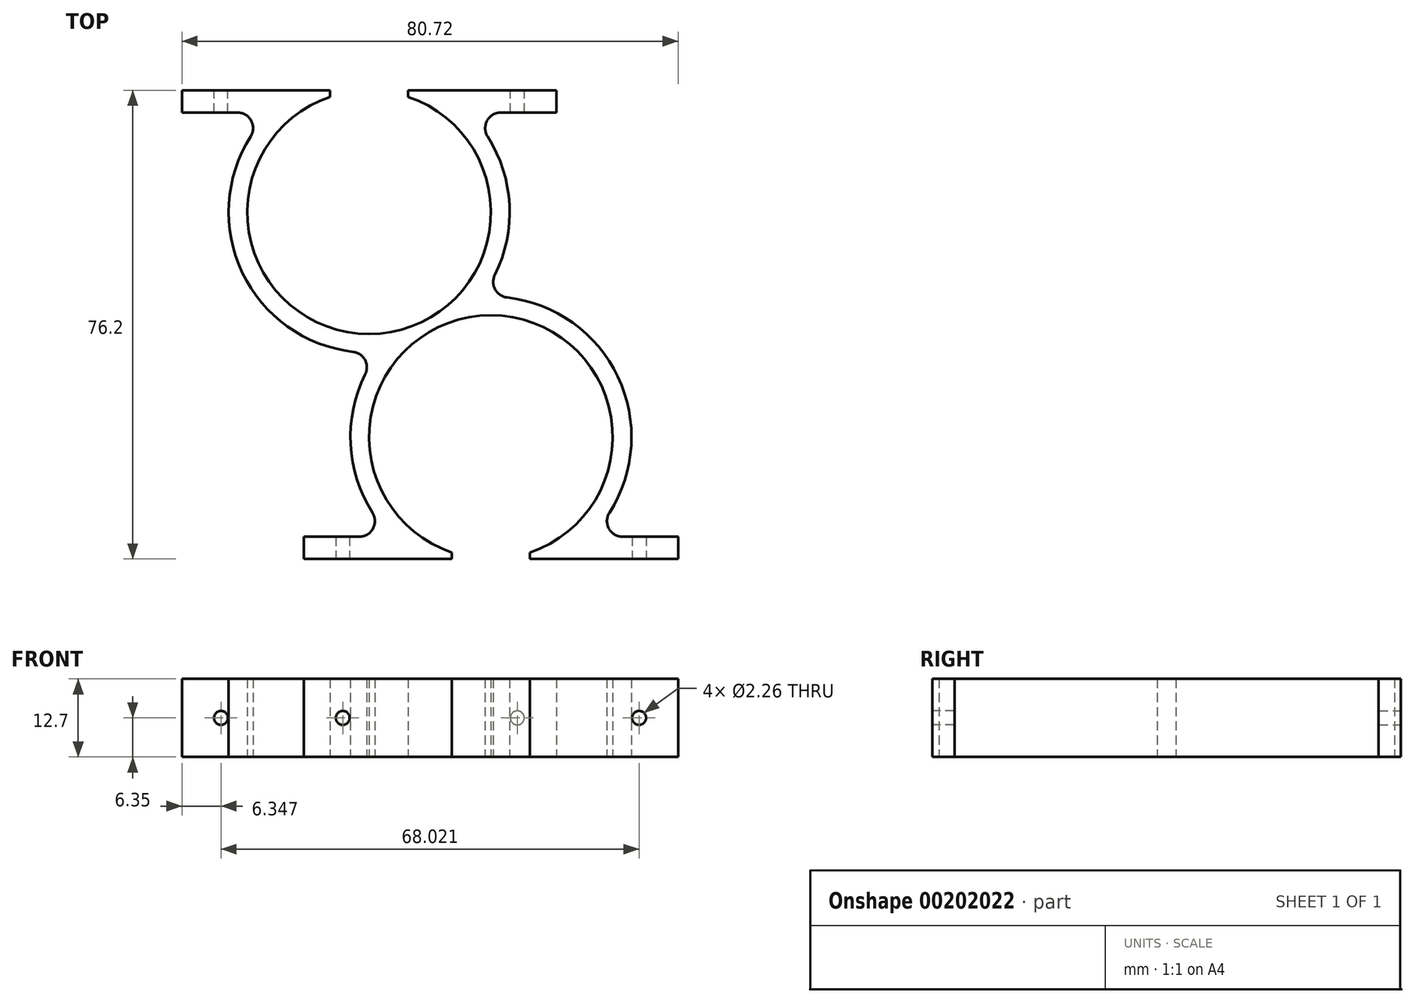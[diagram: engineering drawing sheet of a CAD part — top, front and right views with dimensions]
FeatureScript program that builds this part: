
annotation { "Feature Type Name" : "Feature", "Feature Type Description" : "" }
export const myFeature = defineFeature(function(context is Context, id is Id, definition is map)
    precondition{}
    {
        {
            var Q0;
            Q0=qCreatedBy(makeId("Top.planeOp"),FACE);
            var sketch = newSketch(context, id + "F0", { "sketchPlane" : qUnion([Q0])});
            skLineSegment(sketch, "E0.bottom", {"start": v(50.8, -38.1) * mm, "end": v(19.28, -38.1) * mm});
            skLineSegment(sketch, "E0.top", {"start": v(50.8, 38.1) * mm, "end": v(-0.53, 38.1) * mm});
            skLineSegment(sketch, "E0.left", {"start": v(50.8, -38.1) * mm, "end": v(50.8, 38.1) * mm});
            skLineSegment(sketch, "E0.right", {"start": v(-50.8, -38.1) * mm, "end": v(-50.8, 6.88) * mm});
            skPoint(sketch, "E0.middle", {"position": v(0, 0) * mm});
            skPoint(sketch, "E1.end.orphan", {"position": v(-30.99, 0) * mm});
            skLineSegment(sketch, "E2", {"start": v(-30.99, 38.1) * mm, "end": v(-30.99, 18.29) * mm});
            skArc(sketch, "E3", {"start": v(-37.34, 37.05) * mm, "mid": v(-30.99, -1.52) * mm, "end": v(-24.64, 37.05) * mm});
            skLineSegment(sketch, "E4", {"start": v(-50.8, -38.1) * mm, "end": v(-41.63, -38.1) * mm});
            skLineSegment(sketch, "E5", {"start": v(-11.18, -38.1) * mm, "end": v(-11.18, -18.29) * mm});
            skArc(sketch, "E6", {"start": v(-4.83, -37.05) * mm, "mid": v(-11.18, 1.52) * mm, "end": v(-17.53, -37.05) * mm});
            skArc(sketch, "E7.0", {"start": v(-10.53, 8.08) * mm, "mid": v(-8.16, 19.49) * mm, "end": v(-11.72, 30.58) * mm});
            skArc(sketch, "E8.0", {"start": v(-31.63, -8.08) * mm, "mid": v(-34, -19.49) * mm, "end": v(-30.45, -30.58) * mm});
            skArc(sketch, "E9.trimOffspring", {"start": v(8.1, -30.58) * mm, "mid": v(9.47, -8.47) * mm, "end": v(-8.55, 4.42) * mm});
            skArc(sketch, "E10.trimOffspring", {"start": v(-50.26, 30.58) * mm, "mid": v(-51.63, 8.47) * mm, "end": v(-33.61, -4.42) * mm});
            skPoint(sketch, "E11.visualSharp", {"position": v(-12.74, 4.52) * mm});
            skArc(sketch, "E11.filletArc", {"start": v(-10.53, 8.08) * mm, "mid": v(-10.5, 5.73) * mm, "end": v(-8.55, 4.42) * mm});
            skPoint(sketch, "E12.visualSharp", {"position": v(-29.42, -4.52) * mm});
            skArc(sketch, "E12.filletArc", {"start": v(-31.63, -8.08) * mm, "mid": v(-31.67, -5.73) * mm, "end": v(-33.61, -4.42) * mm});
            skLineSegment(sketch, "E13", {"start": v(-22.58, -38.1) * mm, "end": v(-22.58, -40.64) * mm});
            skLineSegment(sketch, "E14", {"start": v(-22.58, -40.64) * mm, "end": v(-40.26, -40.64) * mm});
            skLineSegment(sketch, "E15", {"start": v(-32.59, -34.49) * mm, "end": v(-41.63, -34.49) * mm});
            skLineSegment(sketch, "E16", {"start": v(-41.63, -34.49) * mm, "end": v(-41.63, -38.1) * mm});
            skLineSegment(sketch, "E17.MirrorCS", {"start": v(4.95, -34.49) * mm, "end": v(19.28, -34.49) * mm});
            skLineSegment(sketch, "E18.MirrorCS", {"start": v(10.24, -34.49) * mm, "end": v(19.28, -34.49) * mm});
            skLineSegment(sketch, "E19.MirrorCS", {"start": v(19.28, -34.49) * mm, "end": v(19.28, -38.1) * mm});
            skLineSegment(sketch, "E20.MirrorCS", {"start": v(28.45, -38.1) * mm, "end": v(19.28, -38.1) * mm});
            skPoint(sketch, "E21.orphan", {"position": v(-22.58, -34.49) * mm});
            skPoint(sketch, "E22.orphan", {"position": v(0.23, -34.49) * mm});
            skPoint(sketch, "E23.MirrorCS.start.orphan", {"position": v(0.23, -38.1) * mm});
            skPoint(sketch, "E24.visualSharp", {"position": v(-27.3, -34.49) * mm});
            skArc(sketch, "E24.filletArc", {"start": v(-32.59, -34.49) * mm, "mid": v(-30.36, -33.17) * mm, "end": v(-30.45, -30.58) * mm});
            skPoint(sketch, "E25.visualSharp", {"position": v(4.95, -34.49) * mm});
            skArc(sketch, "E25.filletArc", {"start": v(8.1, -30.58) * mm, "mid": v(8.01, -33.17) * mm, "end": v(10.24, -34.49) * mm});
            skLineSegment(sketch, "E26", {"start": v(-52.4, 34.49) * mm, "end": v(-61.44, 34.49) * mm});
            skLineSegment(sketch, "E27", {"start": v(-61.44, 38.1) * mm, "end": v(-61.44, 34.49) * mm});
            skLineSegment(sketch, "E28", {"start": v(-9.57, 34.49) * mm, "end": v(-0.53, 34.49) * mm});
            skLineSegment(sketch, "E29", {"start": v(-0.53, 34.49) * mm, "end": v(-0.53, 38.1) * mm});
            skPoint(sketch, "E29.endSnap0", {"position": v(0, 38.1) * mm});
            skPoint(sketch, "E30.visualSharp", {"position": v(-47.12, 34.49) * mm});
            skArc(sketch, "E30.filletArc", {"start": v(-50.26, 30.58) * mm, "mid": v(-50.17, 33.17) * mm, "end": v(-52.4, 34.49) * mm});
            skPoint(sketch, "E31.visualSharp", {"position": v(-14.86, 34.49) * mm});
            skArc(sketch, "E31.filletArc", {"start": v(-9.57, 34.49) * mm, "mid": v(-11.8, 33.17) * mm, "end": v(-11.72, 30.58) * mm});
            skLineSegment(sketch, "E32", {"start": v(-30.99, 18.29) * mm, "end": v(-37.34, 18.29) * mm});
            skLineSegment(sketch, "E33", {"start": v(-37.34, 18.29) * mm, "end": v(-37.34, 38.1) * mm});
            skLineSegment(sketch, "E34.MirrorCS", {"start": v(-24.64, 18.29) * mm, "end": v(-24.64, 38.1) * mm});
            skPoint(sketch, "E35.start.orphan", {"position": v(-50.8, 38.1) * mm});
            skLineSegment(sketch, "E36", {"start": v(-11.18, -18.29) * mm, "end": v(-4.83, -18.29) * mm});
            skLineSegment(sketch, "E37", {"start": v(-4.83, -18.29) * mm, "end": v(-4.83, -38.1) * mm});
            skLineSegment(sketch, "E38.MirrorCS", {"start": v(-17.53, -18.29) * mm, "end": v(-17.53, -38.1) * mm});
            skPoint(sketch, "E39.orphan", {"position": v(-11.18, -38.1) * mm});
            skLineSegment(sketch, "E40.trimOffspring", {"start": v(0.23, -38.1) * mm, "end": v(-4.83, -38.1) * mm});
            skLineSegment(sketch, "E41.trimOffspring", {"start": v(-41.63, -38.1) * mm, "end": v(-50.8, -38.1) * mm});
            skLineSegment(sketch, "E42", {"start": v(-41.63, -38.1) * mm, "end": v(-17.53, -38.1) * mm});
            skLineSegment(sketch, "E43", {"start": v(-4.83, -38.1) * mm, "end": v(19.28, -38.1) * mm});
            skLineSegment(sketch, "E44", {"start": v(-0.53, 38.1) * mm, "end": v(-24.64, 38.1) * mm});
            skLineSegment(sketch, "E45", {"start": v(-61.44, 38.1) * mm, "end": v(-37.34, 38.1) * mm});
            skSolve(sketch);
        }
        {
            var Q0;
            {var subQ1=sQuery(id+"F0.wireOp",EDGE,"E3");Q0=makeQuery(id+"F0.imprint","IMPRINT",FACE,{"disambiguationData":[TD([[makeQuery(id+"F0.imprint","IMPRINT",EDGE,{"derivedFrom":subQ1}),-1.0]])]});}
            extrude(context, id + "F1", {"entities" : qUnion([Q0]), "depth" : 12.7 * mm});
        }
        {
            var Q0;
            Q0=makeQuery(id+"F1.opExtrude","SWEPT_FACE",FACE,{"disambiguationData":[OSD([sQuery(id+"F0.wireOp",EDGE,"E42")])]});
            var sketch = newSketch(context, id + "F2", { "sketchPlane" : qUnion([Q0])});
            skLineSegment(sketch, "E46", {"start": v(-41.63, 12.7) * mm, "end": v(-41.63, 6.35) * mm});
            skLineSegment(sketch, "E47", {"start": v(-41.63, 6.35) * mm, "end": v(-35.28, 6.35) * mm});
            skSolve(sketch);
        }
        {
            var Q0;
            Q0=makeQuery(id+"F1.opExtrude","SWEPT_FACE",FACE,{"disambiguationData":[OSD([sQuery(id+"F0.wireOp",EDGE,"E43")])]});
            var sketch = newSketch(context, id + "F3", { "sketchPlane" : qUnion([Q0])});
            skLineSegment(sketch, "E48", {"start": v(19.28, 12.7) * mm, "end": v(19.28, 6.35) * mm});
            skLineSegment(sketch, "E49", {"start": v(19.28, 6.35) * mm, "end": v(12.93, 6.35) * mm});
            skSolve(sketch);
        }
        {
            var Q0;
            Q0=makeQuery(id+"F1.opExtrude","SWEPT_FACE",FACE,{"disambiguationData":[OSD([sQuery(id+"F0.wireOp",EDGE,"E45")])]});
            var sketch = newSketch(context, id + "F4", { "sketchPlane" : qUnion([Q0])});
            skLineSegment(sketch, "E50", {"start": v(61.44, 0) * mm, "end": v(61.44, 6.35) * mm});
            skLineSegment(sketch, "E51", {"start": v(61.44, 6.35) * mm, "end": v(55.1, 6.35) * mm});
            skSolve(sketch);
        }
        {
            var Q0;
            Q0=makeQuery(id+"F1.opExtrude","SWEPT_FACE",FACE,{"disambiguationData":[OSD([sQuery(id+"F0.wireOp",EDGE,"E44")])]});
            var sketch = newSketch(context, id + "F5", { "sketchPlane" : qUnion([Q0])});
            skLineSegment(sketch, "E52", {"start": v(0.53, 0) * mm, "end": v(0.53, 6.35) * mm});
            skLineSegment(sketch, "E53", {"start": v(0.53, 6.35) * mm, "end": v(6.88, 6.35) * mm});
            skSolve(sketch);
        }
        {
            var Q0;
            Q0=sQuery(id+"F4.wireOp",VERTEX,"E51.end");
            var Q1;
            Q1=sQuery(id+"F5.wireOp",VERTEX,"E53.end");
            var Q2;
            Q2=sQuery(id+"F2.wireOp",VERTEX,"E47.end");
            var Q3;
            Q3=sQuery(id+"F3.wireOp",VERTEX,"E49.end");
            var Q4;
            Q4=makeQuery(id+"F1.opExtrude","SWEPT_BODY",BODY,{"disambiguationData":[OSD([sQuery(id+"F0.wireOp",EDGE,"E3"),sQuery(id+"F0.wireOp",EDGE,"E6"),sQuery(id+"F0.wireOp",EDGE,"E7.0"),sQuery(id+"F0.wireOp",EDGE,"E8.0"),sQuery(id+"F0.wireOp",EDGE,"E9.trimOffspring"),sQuery(id+"F0.wireOp",EDGE,"E10.trimOffspring"),sQuery(id+"F0.wireOp",EDGE,"E11.filletArc"),sQuery(id+"F0.wireOp",EDGE,"E12.filletArc"),sQuery(id+"F0.wireOp",EDGE,"E15"),sQuery(id+"F0.wireOp",EDGE,"E16"),sQuery(id+"F0.wireOp",EDGE,"E18.MirrorCS"),sQuery(id+"F0.wireOp",EDGE,"E19.MirrorCS"),sQuery(id+"F0.wireOp",EDGE,"E24.filletArc"),sQuery(id+"F0.wireOp",EDGE,"E25.filletArc"),sQuery(id+"F0.wireOp",EDGE,"E26"),sQuery(id+"F0.wireOp",EDGE,"E27"),sQuery(id+"F0.wireOp",EDGE,"E28"),sQuery(id+"F0.wireOp",EDGE,"E29"),sQuery(id+"F0.wireOp",EDGE,"E30.filletArc"),sQuery(id+"F0.wireOp",EDGE,"E31.filletArc"),sQuery(id+"F0.wireOp",EDGE,"E33"),sQuery(id+"F0.wireOp",EDGE,"E34.MirrorCS"),sQuery(id+"F0.wireOp",EDGE,"E37"),sQuery(id+"F0.wireOp",EDGE,"E38.MirrorCS"),sQuery(id+"F0.wireOp",EDGE,"E42"),sQuery(id+"F0.wireOp",EDGE,"E43"),sQuery(id+"F0.wireOp",EDGE,"E44"),sQuery(id+"F0.wireOp",EDGE,"E45")])]});
            hole(context, id + "F6", {"style" : HoleStyle.SIMPLE, "endStyle" : HoleEndStyle.BLIND, "standardTappedOrClearance" : lookupTablePath({ "standard" : "ANSI", "fit" : "Close (ASME)", "engagement" : "75%", "pitch" : "40 tpi", "size" : "#4", "type" : "Tapped" }), "standardBlindInLast" : lookupTablePath({ "fit" : "Close", "standard" : "ANSI", "engagement" : "75%", "pitch" : "40 tpi", "size" : "#4", "type" : "Tapped" }), "holeDiameter" : 2.26 * mm, "holeDepth" : 12.7 * mm, "locations" : qUnion([Q0, Q1, Q2, Q3]), "scope" : qUnion([Q4]), "majorDiameter" : 2.84 * mm});
        }
    });
